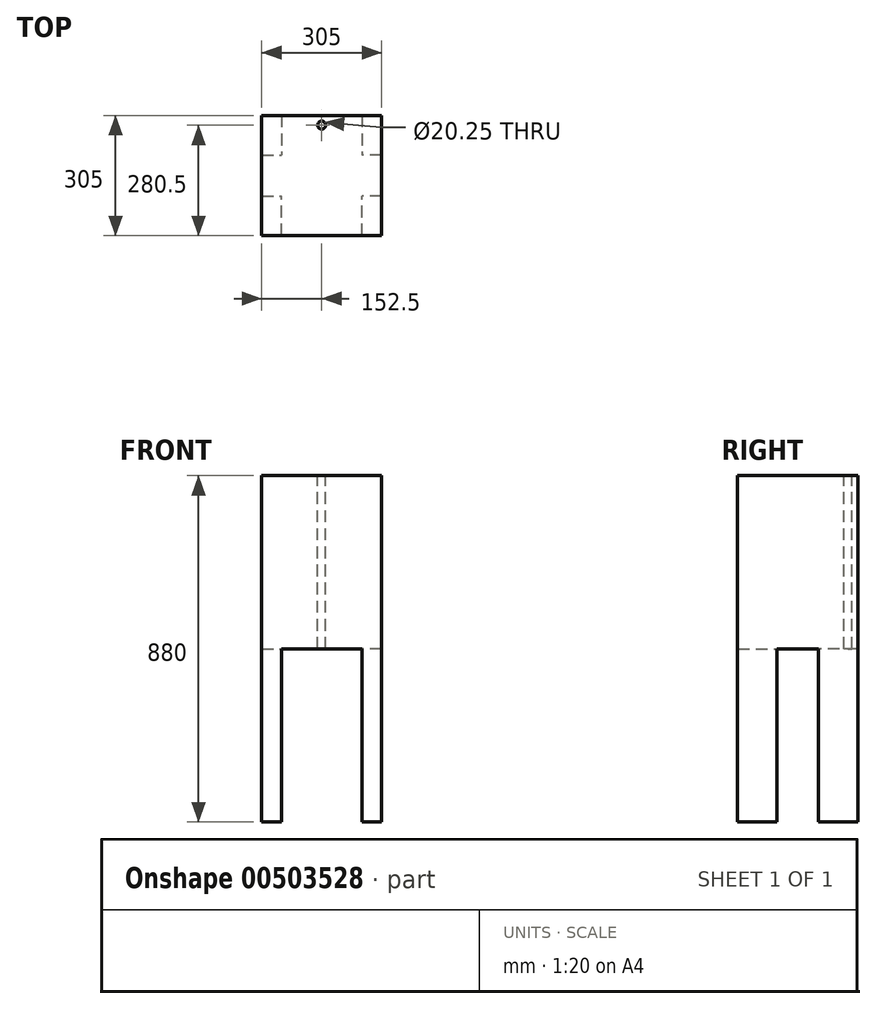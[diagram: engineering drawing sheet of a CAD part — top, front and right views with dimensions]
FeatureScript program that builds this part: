
annotation { "Feature Type Name" : "Feature", "Feature Type Description" : "" }
export const myFeature = defineFeature(function(context is Context, id is Id, definition is map)
    precondition{}
    {
        {
            var Q0;
            Q0=qCreatedBy(makeId("Front.planeOp"),FACE);
            var sketch = newSketch(context, id + "F0", { "sketchPlane" : qUnion([Q0])});
            skLineSegment(sketch, "E0", {"start": v(0, 222.73) * mm, "end": v(0, -217.27) * mm});
            skLineSegment(sketch, "E1", {"start": v(0, 222.73) * mm, "end": v(305, 222.73) * mm});
            skLineSegment(sketch, "E2", {"start": v(305, 222.73) * mm, "end": v(305, -217.27) * mm});
            skLineSegment(sketch, "E3", {"start": v(305, -217.27) * mm, "end": v(0, -217.27) * mm});
            skSolve(sketch);
        }
        {
            var Q0;
            Q0=makeQuery(id+"F0.imprint","IMPRINT",FACE,{"disambiguationData":[TD([[makeQuery(id+"F0.imprint","IMPRINT",EDGE,{"derivedFrom":sQuery(id+"F0.wireOp",EDGE,"E0")}),1.0]])]});
            extrude(context, id + "F1", {"entities" : qUnion([Q0]), "depth" : 305 * mm});
        }
        {
            var Q0;
            Q0=makeQuery(id+"F1.opExtrude","SWEPT_FACE",FACE,{"disambiguationData":[OSD([sQuery(id+"F0.wireOp",EDGE,"E1")])]});
            var sketch = newSketch(context, id + "F2", { "sketchPlane" : qUnion([Q0])});
            skLineSegment(sketch, "E4", {"start": v(0, 0) * mm, "end": v(152.5, 0) * mm});
            skCircle(sketch, "E5", {"center": v(152.5, -24.5) * mm, "radius": 10.12 * mm});
            skSolve(sketch);
        }
        {
            var Q0;
            Q0=sQuery(id+"F2.wireOp",VERTEX,"E5.center");
            var Q1;
            Q1=makeQuery(id+"F1.opExtrude","SWEPT_BODY",BODY,{"disambiguationData":[OSD([sQuery(id+"F0.wireOp",EDGE,"E0"),sQuery(id+"F0.wireOp",EDGE,"E1"),sQuery(id+"F0.wireOp",EDGE,"E2"),sQuery(id+"F0.wireOp",EDGE,"E3")])]});
            hole(context, id + "F3", {"style" : HoleStyle.SIMPLE, "endStyle" : HoleEndStyle.THROUGH, "holeDiameter" : 20.25 * mm, "isTappedThrough" : true, "tappedDepth" : 12 * mm, "tapClearance" : 3, "locations" : qUnion([Q0]), "scope" : qUnion([Q1])});
        }
        {
            var Q0;
            Q0=makeQuery(id+"F1.opExtrude","SWEPT_FACE",FACE,{"disambiguationData":[OSD([sQuery(id+"F0.wireOp",EDGE,"E3")])]});
            var sketch = newSketch(context, id + "F4", { "sketchPlane" : qUnion([Q0])});
            skLineSegment(sketch, "E6.bottom", {"start": v(0, 305) * mm, "end": v(50, 305) * mm});
            skLineSegment(sketch, "E6.top", {"start": v(0, 205) * mm, "end": v(50, 205) * mm});
            skLineSegment(sketch, "E6.left", {"start": v(0, 305) * mm, "end": v(0, 205) * mm});
            skLineSegment(sketch, "E6.right", {"start": v(50, 305) * mm, "end": v(50, 205) * mm});
            skLineSegment(sketch, "E7.bottom", {"start": v(305, 305) * mm, "end": v(255, 305) * mm});
            skLineSegment(sketch, "E7.top", {"start": v(305, 205) * mm, "end": v(255, 205) * mm});
            skLineSegment(sketch, "E7.left", {"start": v(305, 305) * mm, "end": v(305, 205) * mm});
            skLineSegment(sketch, "E7.right", {"start": v(255, 305) * mm, "end": v(255, 205) * mm});
            skLineSegment(sketch, "E8.bottom", {"start": v(0, 0) * mm, "end": v(50, 0) * mm});
            skLineSegment(sketch, "E8.top", {"start": v(0, 100) * mm, "end": v(50, 100) * mm});
            skLineSegment(sketch, "E8.left", {"start": v(0, 0) * mm, "end": v(0, 100) * mm});
            skLineSegment(sketch, "E8.right", {"start": v(50, 0) * mm, "end": v(50, 100) * mm});
            skLineSegment(sketch, "E9.bottom", {"start": v(305, 0) * mm, "end": v(255, 0) * mm});
            skLineSegment(sketch, "E9.top", {"start": v(305, 100) * mm, "end": v(255, 100) * mm});
            skLineSegment(sketch, "E9.left", {"start": v(305, 0) * mm, "end": v(305, 100) * mm});
            skLineSegment(sketch, "E9.right", {"start": v(255, 0) * mm, "end": v(255, 100) * mm});
            skSolve(sketch);
        }
        {
            var Q0;
            Q0=makeQuery(id+"F4.imprint","IMPRINT",FACE,{"disambiguationData":[TD([[makeQuery(id+"F4.imprint","IMPRINT",EDGE,{"derivedFrom":sQuery(id+"F4.wireOp",EDGE,"E6.bottom")}),1.0]])]});
            extrude(context, id + "F5", {"entities" : qUnion([Q0]), "operationType" : NewBodyOperationType.ADD, "depth" : 440 * mm});
        }
        {
            var Q0;
            Q0=makeQuery(id+"F4.imprint","IMPRINT",FACE,{"disambiguationData":[TD([[makeQuery(id+"F4.imprint","IMPRINT",EDGE,{"derivedFrom":sQuery(id+"F4.wireOp",EDGE,"E7.bottom")}),1.0]])]});
            var Q1;
            Q1=makeQuery(id+"F4.imprint","IMPRINT",FACE,{"disambiguationData":[TD([[makeQuery(id+"F4.imprint","IMPRINT",EDGE,{"derivedFrom":sQuery(id+"F4.wireOp",EDGE,"E9.bottom")}),-1.0]])]});
            var Q2;
            Q2=makeQuery(id+"F4.imprint","IMPRINT",FACE,{"disambiguationData":[TD([[makeQuery(id+"F4.imprint","IMPRINT",EDGE,{"derivedFrom":sQuery(id+"F4.wireOp",EDGE,"E8.bottom")}),-1.0]])]});
            extrude(context, id + "F6", {"entities" : qUnion([Q0, Q1, Q2]), "operationType" : NewBodyOperationType.ADD, "depth" : 440 * mm});
        }
    });
